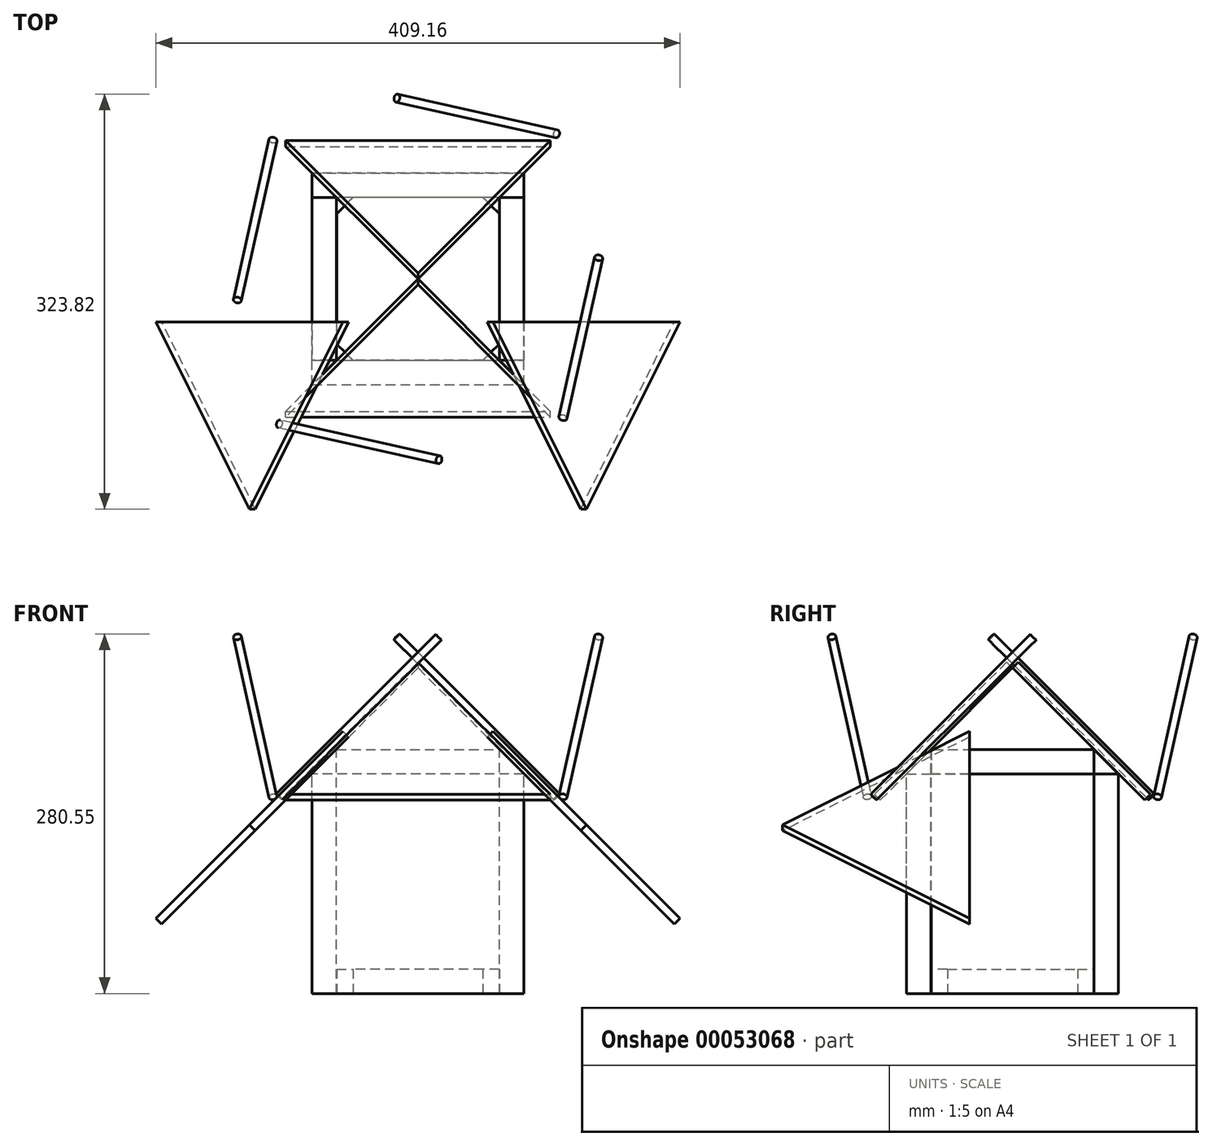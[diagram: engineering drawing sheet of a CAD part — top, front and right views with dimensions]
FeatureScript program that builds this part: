
annotation { "Feature Type Name" : "Feature", "Feature Type Description" : "" }
export const myFeature = defineFeature(function(context is Context, id is Id, definition is map)
    precondition{}
    {
        {
            var Q0;
            Q0=qCreatedBy(makeId("Front.planeOp"),FACE);
            var sketch = newSketch(context, id + "F0", { "sketchPlane" : qUnion([Q0])});
            skLineSegment(sketch, "E0", {"start": v(0, -212.43) * mm, "end": v(0, 255.15) * mm, "construction": true});
            skSolve(sketch);
        }
        {
            var Q0;
            Q0=qCreatedBy(makeId("Top.planeOp"),FACE);
            var sketch = newSketch(context, id + "F1", { "sketchPlane" : qUnion([Q0])});
            skLineSegment(sketch, "E1.rect.bottom", {"start": v(50.8, -63.5) * mm, "end": v(-50.8, -63.5) * mm});
            skLineSegment(sketch, "E1.rect.top", {"start": v(50.8, 63.5) * mm, "end": v(-50.8, 63.5) * mm});
            skLineSegment(sketch, "E1.rect.left", {"start": v(63.5, -50.8) * mm, "end": v(63.5, 50.8) * mm});
            skLineSegment(sketch, "E1.rect.right", {"start": v(-63.5, -50.8) * mm, "end": v(-63.5, 50.8) * mm});
            skPoint(sketch, "E1.rect.middle", {"position": v(0, 0) * mm});
            skLineSegment(sketch, "E2", {"start": v(-63.5, 50.8) * mm, "end": v(-50.8, 63.5) * mm});
            skPoint(sketch, "E3.orphan", {"position": v(-63.5, 63.5) * mm});
            skLineSegment(sketch, "E4.MirrorCS", {"start": v(63.5, 50.8) * mm, "end": v(50.8, 63.5) * mm});
            skLineSegment(sketch, "E5.MirrorCS", {"start": v(-63.5, -50.8) * mm, "end": v(-50.8, -63.5) * mm});
            skLineSegment(sketch, "E6.MirrorCS", {"start": v(63.5, -50.8) * mm, "end": v(50.8, -63.5) * mm});
            skPoint(sketch, "E7.orphan", {"position": v(63.5, 63.5) * mm});
            skPoint(sketch, "E8.orphan", {"position": v(63.5, -63.5) * mm});
            skPoint(sketch, "E9.orphan", {"position": v(-63.5, -63.5) * mm});
            skSolve(sketch);
        }
        {
            var Q0;
            Q0=makeQuery(id+"F1.imprint","IMPRINT",FACE,{"disambiguationData":[TD([[makeQuery(id+"F1.imprint","IMPRINT",EDGE,{"derivedFrom":sQuery(id+"F1.wireOp",EDGE,"E1.rect.bottom")}),-1.0]])]});
            extrude(context, id + "F2", {"entities" : qUnion([Q0]), "depth" : 19.05 * mm});
        }
        {
            var Q0;
            Q0=qCreatedBy(makeId("Right.planeOp"),FACE);
            cPlane(context, id + "F3", {"entities" : qUnion([Q0]), "cplaneType" : CPlaneType.OFFSET, "offset" : 63.55 * mm, "width" : 152.4 * mm, "height" : 152.4 * mm});
        }
        {
            var Q0;
            Q0=qCreatedBy(id+"F3.planeOp",FACE);
            var sketch = newSketch(context, id + "F4", { "sketchPlane" : qUnion([Q0])});
            skLineSegment(sketch, "E10.bottom", {"start": v(-63.5, 0) * mm, "end": v(63.5, 0) * mm});
            skLineSegment(sketch, "E10.top", {"start": v(-63.5, 190.5) * mm, "end": v(63.5, 190.5) * mm});
            skLineSegment(sketch, "E10.left", {"start": v(-63.5, 0) * mm, "end": v(-63.5, 190.5) * mm});
            skLineSegment(sketch, "E10.right", {"start": v(63.5, 0) * mm, "end": v(63.5, 190.5) * mm});
            skSolve(sketch);
        }
        {
            var Q0;
            Q0=makeQuery(id+"F4.imprint","IMPRINT",FACE,{"disambiguationData":[TD([[makeQuery(id+"F4.imprint","IMPRINT",EDGE,{"derivedFrom":sQuery(id+"F4.wireOp",EDGE,"E10.bottom")}),1.0]])]});
            extrude(context, id + "F5", {"entities" : qUnion([Q0]), "depth" : 19.05 * mm});
        }
        {
            var Q0;
            Q0=makeQuery(id+"F5.opExtrude","CAP_EDGE",EDGE,{"disambiguationData":[OSD([sQuery(id+"F4.wireOp",EDGE,"E10.top")])],"isStart":false});
            chamfer(context, id + "F6", {"entities" : qUnion([Q0]), "chamferType" : ChamferType.OFFSET_ANGLE, "width" : 19.05 * mm, "oppositeDirection" : false, "angle" : 45 * degree, "tangentPropagation" : true});
        }
        {
            var Q0;
            Q0=qCreatedBy(makeId("Right.planeOp"),FACE);
            cPlane(context, id + "F7", {"entities" : qUnion([Q0]), "cplaneType" : CPlaneType.OFFSET, "offset" : 63.55 * mm, "oppositeDirection" : true, "width" : 152.4 * mm, "height" : 152.4 * mm});
        }
        {
            var Q0;
            Q0=qCreatedBy(id+"F7.planeOp",FACE);
            var sketch = newSketch(context, id + "F8", { "sketchPlane" : qUnion([Q0])});
            skLineSegment(sketch, "E11.bottom", {"start": v(63.5, 0) * mm, "end": v(-63.5, 0) * mm});
            skLineSegment(sketch, "E11.top", {"start": v(63.5, 190.5) * mm, "end": v(-63.5, 190.5) * mm});
            skLineSegment(sketch, "E11.left", {"start": v(63.5, 0) * mm, "end": v(63.5, 190.5) * mm});
            skLineSegment(sketch, "E11.right", {"start": v(-63.5, 0) * mm, "end": v(-63.5, 190.5) * mm});
            skSolve(sketch);
        }
        {
            var Q0;
            Q0=makeQuery(id+"F8.imprint","IMPRINT",FACE,{"disambiguationData":[TD([[makeQuery(id+"F8.imprint","IMPRINT",EDGE,{"derivedFrom":sQuery(id+"F8.wireOp",EDGE,"E11.bottom")}),-1.0]])]});
            extrude(context, id + "F9", {"entities" : qUnion([Q0]), "operationType" : NewBodyOperationType.ADD, "oppositeDirection" : true, "depth" : 19.05 * mm});
        }
        {
            var Q0;
            Q0=makeQuery(id+"F9.opExtrude","CAP_EDGE",EDGE,{"disambiguationData":[OSD([sQuery(id+"F8.wireOp",EDGE,"E11.top")])],"isStart":false});
            chamfer(context, id + "F10", {"entities" : qUnion([Q0]), "chamferType" : ChamferType.OFFSET_ANGLE, "width" : 19.05 * mm, "oppositeDirection" : false, "angle" : 45 * degree, "tangentPropagation" : true});
        }
        {
            var Q0;
            Q0=qCreatedBy(makeId("Front.planeOp"),FACE);
            cPlane(context, id + "F11", {"entities" : qUnion([Q0]), "cplaneType" : CPlaneType.OFFSET, "offset" : 63.55 * mm, "oppositeDirection" : true, "width" : 152.4 * mm, "height" : 152.4 * mm});
        }
        {
            var Q0;
            Q0=qCreatedBy(id+"F11.planeOp",FACE);
            var sketch = newSketch(context, id + "F12", { "sketchPlane" : qUnion([Q0])});
            skLineSegment(sketch, "E12.bottom", {"start": v(82.6, 0) * mm, "end": v(-82.6, 0) * mm});
            skLineSegment(sketch, "E12.top", {"start": v(63.55, 190.5) * mm, "end": v(-63.55, 190.5) * mm});
            skLineSegment(sketch, "E12.left", {"start": v(82.6, 0) * mm, "end": v(82.6, 171.45) * mm});
            skLineSegment(sketch, "E12.right", {"start": v(-82.6, 0) * mm, "end": v(-82.6, 171.45) * mm});
            skLineSegment(sketch, "E13", {"start": v(-82.6, 171.45) * mm, "end": v(-63.55, 190.5) * mm});
            skLineSegment(sketch, "E14", {"start": v(82.6, 171.45) * mm, "end": v(63.55, 190.5) * mm});
            skSolve(sketch);
        }
        {
            var Q0;
            Q0=makeQuery(id+"F12.imprint","IMPRINT",FACE,{"disambiguationData":[TD([[makeQuery(id+"F12.imprint","IMPRINT",EDGE,{"derivedFrom":sQuery(id+"F12.wireOp",EDGE,"E12.bottom")}),-1.0]])]});
            extrude(context, id + "F13", {"entities" : qUnion([Q0]), "oppositeDirection" : true, "depth" : 19.05 * mm});
        }
        {
            var Q0;
            Q0=makeQuery(id+"F13.opExtrude","CAP_EDGE",EDGE,{"disambiguationData":[OSD([sQuery(id+"F12.wireOp",EDGE,"E12.top")])],"isStart":false});
            chamfer(context, id + "F14", {"entities" : qUnion([Q0]), "chamferType" : ChamferType.OFFSET_ANGLE, "width" : 19.05 * mm, "oppositeDirection" : false, "angle" : 45 * degree, "tangentPropagation" : true});
        }
        {
            var Q0;
            Q0=qCreatedBy(makeId("Front.planeOp"),FACE);
            cPlane(context, id + "F15", {"entities" : qUnion([Q0]), "cplaneType" : CPlaneType.OFFSET, "offset" : 63.55 * mm, "width" : 152.4 * mm, "height" : 152.4 * mm});
        }
        {
            var Q0;
            Q0=qCreatedBy(id+"F15.planeOp",FACE);
            var sketch = newSketch(context, id + "F16", { "sketchPlane" : qUnion([Q0])});
            skLineSegment(sketch, "E15.bottom", {"start": v(-82.6, 0) * mm, "end": v(82.6, 0) * mm});
            skLineSegment(sketch, "E15.top", {"start": v(-63.55, 190.5) * mm, "end": v(63.55, 190.5) * mm});
            skLineSegment(sketch, "E15.left", {"start": v(-82.6, 0) * mm, "end": v(-82.6, 171.45) * mm});
            skLineSegment(sketch, "E15.right", {"start": v(82.6, 0) * mm, "end": v(82.6, 171.45) * mm});
            skLineSegment(sketch, "E16", {"start": v(-82.6, 171.45) * mm, "end": v(-63.55, 190.5) * mm});
            skLineSegment(sketch, "E17", {"start": v(82.6, 171.45) * mm, "end": v(63.55, 190.5) * mm});
            skPoint(sketch, "E18.orphan", {"position": v(-82.6, 190.5) * mm});
            skPoint(sketch, "E19.orphan", {"position": v(82.6, 190.5) * mm});
            skSolve(sketch);
        }
        {
            var Q0;
            Q0=makeQuery(id+"F16.imprint","IMPRINT",FACE,{"disambiguationData":[TD([[makeQuery(id+"F16.imprint","IMPRINT",EDGE,{"derivedFrom":sQuery(id+"F16.wireOp",EDGE,"E15.bottom")}),1.0]])]});
            extrude(context, id + "F17", {"entities" : qUnion([Q0]), "depth" : 19.05 * mm});
        }
        {
            var Q0;
            Q0=makeQuery(id+"F17.opExtrude","CAP_EDGE",EDGE,{"disambiguationData":[OSD([sQuery(id+"F16.wireOp",EDGE,"E15.top")])],"isStart":false});
            chamfer(context, id + "F18", {"entities" : qUnion([Q0]), "chamferType" : ChamferType.OFFSET_ANGLE, "width" : 19.05 * mm, "oppositeDirection" : false, "angle" : 45 * degree, "tangentPropagation" : true});
        }
        {
            var Q0;
            Q0=makeQuery(id+"F6.opChamfer","BLEND_FACE",FACE,{"disambiguationData":[OSD([sQuery(id+"F4.wireOp",EDGE,"E10.top")])]});
            cPlane(context, id + "F19", {"entities" : qUnion([Q0]), "cplaneType" : CPlaneType.OFFSET, "offset" : 0.05 * mm, "width" : 152.4 * mm, "height" : 152.4 * mm});
        }
        {
            var Q0;
            Q0=qCreatedBy(id+"F19.planeOp",FACE);
            var sketch = newSketch(context, id + "F20", { "sketchPlane" : qUnion([Q0])});
            skLineSegment(sketch, "E20", {"start": v(-219.22, 0) * mm, "end": v(55.85, 0) * mm, "construction": true});
            skLineSegment(sketch, "E21", {"start": v(-179.7, 108.89) * mm, "end": v(-179.7, -115.2) * mm, "construction": true});
            skLineSegment(sketch, "E22", {"start": v(-179.64, 0) * mm, "end": v(-33.6, -103.27) * mm});
            skLineSegment(sketch, "E23", {"start": v(-33.6, -103.27) * mm, "end": v(-33.6, 103.27) * mm});
            skLineSegment(sketch, "E24", {"start": v(-33.6, 103.27) * mm, "end": v(-179.64, 0) * mm});
            skSolve(sketch);
        }
        {
            var Q0;
            Q0=makeQuery(id+"F20.imprint","IMPRINT",FACE,{"disambiguationData":[TD([[makeQuery(id+"F20.imprint","IMPRINT",EDGE,{"derivedFrom":sQuery(id+"F20.wireOp",EDGE,"E22")}),1.0]])]});
            extrude(context, id + "F21", {"entities" : qUnion([Q0]), "depth" : 6.35 * mm});
        }
        {
            var Q0;
            Q0=makeQuery(id+"F21.opExtrude","SWEPT_BODY",BODY,{"disambiguationData":[OSD([sQuery(id+"F20.wireOp",EDGE,"E22"),sQuery(id+"F20.wireOp",EDGE,"E23"),sQuery(id+"F20.wireOp",EDGE,"E24")])]});
            var Q1;
            Q1=qCreatedBy(makeId("Right.planeOp"),FACE);
            mirror(context, id + "F22", {"entities" : qUnion([Q0]), "mirrorPlane" : qUnion([Q1])});
        }
        {
            var Q0;
            Q0=makeQuery(id+"F18.opChamfer","BLEND_FACE",FACE,{"disambiguationData":[OSD([sQuery(id+"F16.wireOp",EDGE,"E15.top")])]});
            cPlane(context, id + "F23", {"entities" : qUnion([Q0]), "cplaneType" : CPlaneType.OFFSET, "offset" : 0.1 * mm, "width" : 152.4 * mm, "height" : 152.4 * mm});
        }
        {
            var Q0;
            Q0=qCreatedBy(id+"F23.planeOp",FACE);
            var sketch = newSketch(context, id + "F24", { "sketchPlane" : qUnion([Q0])});
            skLineSegment(sketch, "E25", {"start": v(-103.27, 33.6) * mm, "end": v(103.27, 33.6) * mm});
            skLineSegment(sketch, "E26", {"start": v(103.27, 33.6) * mm, "end": v(0, 179.64) * mm});
            skLineSegment(sketch, "E27", {"start": v(0, 179.64) * mm, "end": v(-103.27, 33.6) * mm});
            skLineSegment(sketch, "E28", {"start": v(0, 190) * mm, "end": v(0, -67.7) * mm, "construction": true});
            skLineSegment(sketch, "E29", {"start": v(-159.49, 179.74) * mm, "end": v(154.86, 179.74) * mm, "construction": true});
            skSolve(sketch);
        }
        {
            var Q0;
            Q0=makeQuery(id+"F24.imprint","IMPRINT",FACE,{"disambiguationData":[TD([[makeQuery(id+"F24.imprint","IMPRINT",EDGE,{"derivedFrom":sQuery(id+"F24.wireOp",EDGE,"E25")}),1.0]])]});
            extrude(context, id + "F25", {"entities" : qUnion([Q0]), "depth" : 6.35 * mm});
        }
        {
            var Q0;
            Q0=makeQuery(id+"F25.opExtrude","SWEPT_BODY",BODY,{"disambiguationData":[OSD([sQuery(id+"F24.wireOp",EDGE,"E25"),sQuery(id+"F24.wireOp",EDGE,"E26"),sQuery(id+"F24.wireOp",EDGE,"E27")])]});
            var Q1;
            Q1=qCreatedBy(makeId("Front.planeOp"),FACE);
            mirror(context, id + "F26", {"entities" : qUnion([Q0]), "mirrorPlane" : qUnion([Q1])});
        }
        {
            var Q0;
            Q0=makeQuery(id+"F25.opExtrude","CAP_VERTEX",VERTEX,{"disambiguationData":[OSD([sQuery(id+"F24.wireOp",EDGE,"E25"),sQuery(id+"F24.wireOp",EDGE,"E26")])],"isStart":true});
            var Q1;
            Q1=makeQuery(id+"F25.opExtrude","CAP_VERTEX",VERTEX,{"disambiguationData":[OSD([sQuery(id+"F24.wireOp",EDGE,"E25"),sQuery(id+"F24.wireOp",EDGE,"E26")])],"isStart":false});
            var Q2;
            Q2=makeQuery(id+"F21.opExtrude","CAP_VERTEX",VERTEX,{"disambiguationData":[OSD([sQuery(id+"F20.wireOp",EDGE,"E22"),sQuery(id+"F20.wireOp",EDGE,"E23")])],"isStart":false});
            cPlane(context, id + "F27", {"entities" : qUnion([Q0, Q1, Q2]), "cplaneType" : CPlaneType.THREE_POINT, "offset" : 152.4 * mm, "width" : 152.4 * mm, "height" : 152.4 * mm});
        }
        {
            var Q0;
            Q0=qCreatedBy(id+"F27.planeOp",FACE);
            var sketch = newSketch(context, id + "F28", { "sketchPlane" : qUnion([Q0])});
            skCircle(sketch, "E30", {"center": v(106.9, 185.14) * mm, "radius": 3.18 * mm});
            skSolve(sketch);
        }
        {
            var Q0;
            Q0=makeQuery(id+"F28.imprint","IMPRINT",FACE,{"disambiguationData":[TD([[makeQuery(id+"F28.imprint","IMPRINT",EDGE,{"derivedFrom":sQuery(id+"F28.wireOp",EDGE,"E30")}),1.0]])]});
            extrude(context, id + "F29", {"entities" : qUnion([Q0]), "oppositeDirection" : true, "depth" : 178.56 * mm});
        }
        {
            var Q0;
            Q0=makeQuery(id+"F29.opExtrude","SWEPT_BODY",BODY,{"disambiguationData":[OSD([sQuery(id+"F28.wireOp",EDGE,"E30")])]});
            var Q1;
            Q1=sQuery(id+"F0.wireOp",EDGE,"E0");
            circularPattern(context, id + "F30", {"entities" : qUnion([Q0]), "axis" : qUnion([Q1]), "angle" : 90 * degree, "instanceCount" : 4});
        }
    });
